# Revit family: Flooring_Entrance-Flooring_emco_MARSCHALL-Premium
name_source: partatom
category: Furniture Systems
revit_build: Autodesk Revit 2018 (Build: 20190510_1515(x64)
units: mm (PartAtom-declared; Revit-internal decimal feet)

## family parameters
Cut with Voids When Loaded = No
Host = Face
OmniClass Number = 23.15.17.11.11
OmniClass Title = Floor Toppings
Part Type = Normal
Room Calculation Point = No
Round Connector Dimension = Use Diameter
Shared = No

## types (69) — shared parameters
Assembly Code = E2010400
Date Updated = 2023/08/22
Default Elevation = 1219 mm
Description = Rollable and hard-wearing premium entrance mat with performance insert for supported installation options.
Keynote = 12480.A1
Manufacturer = Emco
Product data url = https://bimobject.com
Profile Material = Emco - Metal - Aluminium
Standard profile clearance approx. (mm) = 5 mm, rubber spacers
URL = https://www.emco-bau.com
Version = 1

## per-type parameters (varying)
| type | Brush strip | Colour fastness to artificial light ISO 105-B02 | Colour fastness to rubbing ISO 105 X12 | Colour fastness to water ISO 105 E01 | EPIMID | Flammability | Height 12 | Height 17 | Height 22 | Large | Normal | Pile material | Profile width (mm) | Scraping edge | Slip resistance | Tread surface | Weight (kg/m2) | z_Height | z_edge_height | z_insert_offset | z_insert_width | z_slot_offest | z_slot_width |
| Large With Care insert 512 PSL Care | No | good 5-6 | good 4-5 | good 4-5 | 99905 | Fire classification for the complete mat system Cfl-s1 in accordance with EN 13501 | Yes | No | No | Yes | No | 100% PA 6 (polyamide) | 46.5 mm | No | R 12 slip resistance as per DIN 51130 | The robust and exceptionally abrasion-resistant Care insert for the effective reduction of fine dirt. | 10.6 | 12 mm  [stored 0.0393701 ft] | 16 mm | 52 mm | 47 mm | 49 mm | 5 mm  [stored 0.0164042 ft] |
| Large With Care insert 517 PSL Care | No | good 5-6 | good 4-5 | good 4-5 | 99907 | Fire classification for the complete mat system Cfl-s1 in accordance with EN 13501 | No | Yes | No | Yes | No | 100% PA 6 (polyamide) | 46.5 mm | No | R 12 slip resistance as per DIN 51130 | The robust and exceptionally abrasion-resistant Care insert for the effective reduction of fine dirt. | 131 | 17 mm | 20 mm  [stored 0.0656168 ft] | 52 mm | 47 mm | 49 mm | 5 mm  [stored 0.0164042 ft] |
| Large With Conform insert 512 PSL Conform | No | - | - | - | 99911 | Fire classification for the complete mat system Cfl-s1 in accordance with EN 13501 | Yes | No | No | Yes | No | 100% PA 6 (polyamide) | 46.5 mm | No | R 12 slip resistance as per DIN 51130 | The Conform insert made of recycled materials is the perfect complement to wooden surroundings and can be used in a whole host of environments. | 10.8 | 12 mm  [stored 0.0393701 ft] | 16 mm | 52 mm | 47 mm | 49 mm | 5 mm  [stored 0.0164042 ft] |
| Large With Conform insert 517 PSL Conform | No | - | - | - | 99913 | Fire classification for the complete mat system Cfl-s1 in accordance with EN 13501 | No | Yes | No | Yes | No | 100% PA 6 (polyamide) | 46.5 mm | No | R 12 slip resistance as per DIN 51130 | The Conform insert made of recycled materials is the perfect complement to wooden surroundings and can be used in a whole host of environments. | 13.8 | 17 mm | 20 mm  [stored 0.0656168 ft] | 52 mm | 47 mm | 49 mm | 5 mm  [stored 0.0164042 ft] |
| Large With Conform insert 522 PSL Conform | No | - | - | - | 99915 | Fire classification for the complete mat system Cfl-s1 in accordance with EN 13501 | No | No | Yes | Yes | No | 100% PA 6 (polyamide) | 46.5 mm | No | R 12 slip resistance as per DIN 51130 | The Conform insert made of recycled materials is the perfect complement to wooden surroundings and can be used in a whole host of environments. | 14.5 | 22 mm  [stored 0.0721785 ft] | 25 mm  [stored 0.082021 ft] | 52 mm | 47 mm | 49 mm | 5 mm  [stored 0.0164042 ft] |
| Large With Conform insert and brush strip 517 PSL Conform B | Yes | - | - | - | 105831 | Insert with fire classification Cfl-s1 according to EN 13501. | No | Yes | No | Yes | No | 100% PA 6 (polyamide) | 46.5 mm | No | - | The Conform insert made of recycled materials is the perfect complement to wooden surroundings and can be used in a whole host of environments. The additional profile increases the cleaning power. | 131 | 17 mm | 20 mm  [stored 0.0656168 ft] | 66 mm | 47 mm | 56 mm | 20 mm  [stored 0.0656168 ft] |
| Large With Conform insert and brush strip 522 PSL Conform B | Yes | - | - | - | 105832 | Insert with fire classification Cfl-s1 according to EN 13501. | No | No | Yes | Yes | No | 100% PA 6 (polyamide) | 46.5 mm | No | - | The Conform insert made of recycled materials is the perfect complement to wooden surroundings and can be used in a whole host of environments. The additional profile increases the cleaning power. | 14.5 | 22 mm  [stored 0.0721785 ft] | 25 mm  [stored 0.082021 ft] | 66 mm | 47 mm | 56 mm | 20 mm  [stored 0.0656168 ft] |
| Large With Conform insert and scraping edge 512 PSL Conform K | No | - | - | - | 105828 | Insert with fire classification Cfl-s1 according to EN 13501. | Yes | No | No | Yes | No | 100% PA 6 (polyamide) | 46.5 mm | Yes | - | The Conform insert made of recycled materials is the perfect complement to wooden surroundings and can be used in a whole host of environments. The additional profile increases the cleaning power. | 10.5 | 12 mm  [stored 0.0393701 ft] | 16 mm | 62 mm | 47 mm | 54 mm | 15 mm  [stored 0.0492126 ft] |
| Large With Conform insert and scraping edge 517 PSL Conform K | No | - | - | - | 105829 | Insert with fire classification Cfl-s1 according to EN 13501. | No | Yes | No | Yes | No | 100% PA 6 (polyamide) | 46.5 mm | Yes | - | The Conform insert made of recycled materials is the perfect complement to wooden surroundings and can be used in a whole host of environments. The additional profile increases the cleaning power. | 13.4 | 17 mm | 20 mm  [stored 0.0656168 ft] | 62 mm | 47 mm | 54 mm | 15 mm  [stored 0.0492126 ft] |
| Large With Conform insert and scraping edge 522 PSL Conform K | No | - | - | - | 105830 | Insert with fire classification Cfl-s1 according to EN 13501. | No | No | Yes | Yes | No | 100% PA 6 (polyamide) | 46.5 mm | Yes | - | The Conform insert made of recycled materials is the perfect complement to wooden surroundings and can be used in a whole host of environments. The additional profile increases the cleaning power. | 15.2 | 22 mm  [stored 0.0721785 ft] | 25 mm  [stored 0.082021 ft] | 62 mm | 47 mm | 54 mm | 15 mm  [stored 0.0492126 ft] |
| Large With Innova insert 512 PSL Innova | No | good 5-6 | good 4-5 | good 4-5 | 99917 | Fire classification for the complete mat system Cfl-s1 in accordance with EN 13501 | Yes | No | No | Yes | No | 100% PA 6 (polyamide) | 46.5 mm | No | R 12 slip resistance as per DIN 51130 | The exceptionally flexible Innova insert not only creates a sophisticated impression but also improves room acoustics. | 10.9 | 12 mm  [stored 0.0393701 ft] | 16 mm | 52 mm | 47 mm | 49 mm | 5 mm  [stored 0.0164042 ft] |
| Large With Innova insert 517 PSL Innova | No | good 5-6 | good 4-5 | good 4-5 | 99919 | Fire classification for the complete mat system Cfl-s1 in accordance with EN 13501 | No | Yes | No | Yes | No | 100% PA 6 (polyamide) | 46.5 mm | No | R 12 slip resistance as per DIN 51130 | The exceptionally flexible Innova insert not only creates a sophisticated impression but also improves room acoustics. | 12.9 | 17 mm | 20 mm  [stored 0.0656168 ft] | 52 mm | 47 mm | 49 mm | 5 mm  [stored 0.0164042 ft] |
| Large With Innova insert 522 PSL Innova | No | good 5-6 | good 4-5 | good 4-5 | 99921 | Fire classification for the complete mat system Cfl-s1 in accordance with EN 13501 | No | No | Yes | Yes | No | 100% PA 6 (polyamide) | 46.5 mm | No | R 12 slip resistance as per DIN 51130 | The exceptionally flexible Innova insert not only creates a sophisticated impression but also improves room acoustics. | 141 | 22 mm  [stored 0.0721785 ft] | 25 mm  [stored 0.082021 ft] | 52 mm | 47 mm | 49 mm | 5 mm  [stored 0.0164042 ft] |
| Large With Innova insert and brush strip 517 PSL Innova B | Yes | - | - | - | 105841 | Insert with fire classification Cfl-s1 according to EN 13501. | No | Yes | No | Yes | No | 100% PA 6 (polyamide) | 46.5 mm | No | - | The exceptionally flexible Innova insert not only creates a sophisticated impression but also improves room acoustics. The additional profile increases the cleaning power. | 12.8 | 17 mm | 20 mm  [stored 0.0656168 ft] | 66 mm | 47 mm | 56 mm | 20 mm  [stored 0.0656168 ft] |
| Large With Innova insert and brush strip 522 PSL Innova B | Yes | - | - | - | 105842 | Insert with fire classification Cfl-s1 according to EN 13501. | No | No | Yes | Yes | No | 100% PA 6 (polyamide) | 46.5 mm | No | - | The exceptionally flexible Innova insert not only creates a sophisticated impression but also improves room acoustics. The additional profile increases the cleaning power. | 142 | 22 mm  [stored 0.0721785 ft] | 25 mm  [stored 0.082021 ft] | 66 mm | 47 mm | 56 mm | 20 mm  [stored 0.0656168 ft] |
| Large With Innova insert and scraping edge 512 PSL Innova K | No | - | - | - | 105838 | Insert with fire classification Cfl-s1 according to EN 13501. | Yes | No | No | Yes | No | 100% PA 6 (polyamide) | 46.5 mm | Yes | - | The exceptionally flexible Innova insert not only creates a sophisticated impression but also improves room acoustics. The additional profile increases the cleaning power. | 10.3 | 12 mm  [stored 0.0393701 ft] | 16 mm | 62 mm | 47 mm | 54 mm | 15 mm  [stored 0.0492126 ft] |
| Large With Innova insert and scraping edge 517 PSL Innova K | No | - | - | - | 105839 | Insert with fire classification Cfl-s1 according to EN 13501. | No | Yes | No | Yes | No | 100% PA 6 (polyamide) | 46.5 mm | Yes | - | The exceptionally flexible Innova insert not only creates a sophisticated impression but also improves room acoustics. The additional profile increases the cleaning power. | 131 | 17 mm | 20 mm  [stored 0.0656168 ft] | 62 mm | 47 mm | 54 mm | 15 mm  [stored 0.0492126 ft] |
| Large With Innova insert and scraping edge 522 PSL Innova K | No | - | - | - | 105840 | Insert with fire classification Cfl-s1 according to EN 13501. | No | No | Yes | Yes | No | 100% PA 6 (polyamide) | 46.5 mm | Yes | - | The exceptionally flexible Innova insert not only creates a sophisticated impression but also improves room acoustics. The additional profile increases the cleaning power. | 14.9 | 22 mm  [stored 0.0721785 ft] | 25 mm  [stored 0.082021 ft] | 62 mm | 47 mm | 54 mm | 15 mm  [stored 0.0492126 ft] |
| Large With Maximus insert and brush strip 517 PSL Maximus B | Yes | - | - | - | 105819 | Insert with fire classification Bfl-s1 according to EN 13501. | No | Yes | No | Yes | No | 100% PA 6.6 (polyamide) | 46.5 mm | No | - | Embedded, robust MAXIMUS inserts in Bfl-S1 quality (clean-off floor covering made from special polyamide yarn, 100%) | 13 | 17 mm | 20 mm  [stored 0.0656168 ft] | 66 mm | 47 mm | 56 mm | 20 mm  [stored 0.0656168 ft] |
| Large With Maximus insert and brush strip 517 PSL Maximus Image B | Yes | - | - | - | 105820 | Insert with fire classification Bfl-s1 according to EN 13501. | No | Yes | No | Yes | No | 100% PA 6.6 (polyamide) | 46.5 mm | No | - | Embedded, robust MAXIMUS inserts in Bfl-S1 quality (clean-off floor covering made from special polyamide yarn, 100%) | 13 | 17 mm | 20 mm  [stored 0.0656168 ft] | 66 mm | 47 mm | 56 mm | 20 mm  [stored 0.0656168 ft] |
| Large With Maximus insert and brush strip 522 PSL Maximus B | Yes | - | - | - | 105821 | Insert with fire classification Bfl-s1 according to EN 13501. | No | No | Yes | Yes | No | 100% PA 6.6 (polyamide) | 46.5 mm | No | - | Embedded, robust MAXIMUS inserts in Bfl-S1 quality (clean-off floor covering made from special polyamide yarn, 100%) | 14.4 | 22 mm  [stored 0.0721785 ft] | 25 mm  [stored 0.082021 ft] | 66 mm | 47 mm | 56 mm | 20 mm  [stored 0.0656168 ft] |
| Large With Maximus insert and brush strip 522 PSL Maximus Image B | Yes | - | - | - | 105822 | Insert with fire classification Bfl-s1 according to EN 13501. | No | No | Yes | Yes | No | 100% PA 6.6 (polyamide) | 46.5 mm | No | - | Embedded, robust MAXIMUS inserts in Bfl-S1 quality (clean-off floor covering made from special polyamide yarn, 100%) | 14.4 | 22 mm  [stored 0.0721785 ft] | 25 mm  [stored 0.082021 ft] | 66 mm | 47 mm | 56 mm | 20 mm  [stored 0.0656168 ft] |
| Large With Maximus insert and scraping edge 512 PSL Maximus Image K | No | - | - | - | 105814 | Insert with fire classification Bfl-s1 according to EN 13501. | Yes | No | No | Yes | No | 100% PA 6.6 (polyamide) | 46.5 mm | Yes | - | Embedded, robust MAXIMUS inserts in Bfl-S1 quality (clean-off floor covering made from special polyamide yarn, 100%) | 10.9 | 12 mm  [stored 0.0393701 ft] | 16 mm | 62 mm | 47 mm | 54 mm | 15 mm  [stored 0.0492126 ft] |
| Large With Maximus insert and scraping edge 512 PSL Maximus K | No | - | - | - | 105813 | Insert with fire classification Bfl-s1 according to EN 13501. | Yes | No | No | Yes | No | 100% PA 6.6 (polyamide) | 46.5 mm | Yes | - | Embedded, robust MAXIMUS inserts in Bfl-S1 quality (clean-off floor covering made from special polyamide yarn, 100%) | 10.9 | 12 mm  [stored 0.0393701 ft] | 16 mm | 62 mm | 47 mm | 54 mm | 15 mm  [stored 0.0492126 ft] |
| Large With Maximus insert and scraping edge 517 PSL Maximus Image K | No | - | - | - | 105816 | Insert with fire classification Bfl-s1 according to EN 13501. | No | Yes | No | Yes | No | 100% PA 6.6 (polyamide) | 46.5 mm | Yes | - | Embedded, robust MAXIMUS inserts in Bfl-S1 quality (clean-off floor covering made from special polyamide yarn, 100%) | 13.9 | 17 mm | 20 mm  [stored 0.0656168 ft] | 62 mm | 47 mm | 54 mm | 15 mm  [stored 0.0492126 ft] |
| Large With Maximus insert and scraping edge 517 PSL Maximus K | No | - | - | - | 105815 | Insert with fire classification Bfl-s1 according to EN 13501. | No | Yes | No | Yes | No | 100% PA 6.6 (polyamide) | 46.5 mm | Yes | - | Embedded, robust MAXIMUS inserts in Bfl-S1 quality (clean-off floor covering made from special polyamide yarn, 100%) | 13.9 | 17 mm | 20 mm  [stored 0.0656168 ft] | 62 mm | 47 mm | 54 mm | 15 mm  [stored 0.0492126 ft] |
| Large With Maximus insert and scraping edge 522 PSL Maximus Image K | No | - | - | - | 105818 | Insert with fire classification Bfl-s1 according to EN 13501. | No | No | Yes | Yes | No | 100% PA 6.6 (polyamide) | 46.5 mm | Yes | - | Embedded, robust MAXIMUS inserts in Bfl-S1 quality (clean-off floor covering made from special polyamide yarn, 100%) | 15.8 | 22 mm  [stored 0.0721785 ft] | 25 mm  [stored 0.082021 ft] | 62 mm | 47 mm | 54 mm | 15 mm  [stored 0.0492126 ft] |
| Large With Maximus insert and scraping edge 522 PSL Maximus K | No | - | - | - | 105817 | Insert with fire classification Bfl-s1 according to EN 13501. | No | No | Yes | Yes | No | 100% PA 6.6 (polyamide) | 46.5 mm | Yes | - | Embedded, robust MAXIMUS inserts in Bfl-S1 quality (clean-off floor covering made from special polyamide yarn, 100%) | 15.8 | 22 mm  [stored 0.0721785 ft] | 25 mm  [stored 0.082021 ft] | 62 mm | 47 mm | 54 mm | 15 mm  [stored 0.0492126 ft] |
| Large With Outdoor insert 512 PSL Outdoor | No | excellent 7 | good 4-5 | good 4-5 | 99931 | Fire classification for the complete mat system Cfl-s1 in accordance with EN 13501 | Yes | No | No | Yes | No | 100% PA 6 (polyamide) | 46.5 mm | No | R 11 slip resistance as per DIN 51130 | The weather-resistant Outdoor insert for noticeably thorough removal of coarse dirt. | 10.1 | 12 mm  [stored 0.0393701 ft] | 16 mm | 52 mm | 47 mm | 49 mm | 5 mm  [stored 0.0164042 ft] |
| Large With Outdoor insert 517 PSL Outdoor | No | excellent 7 | good 4-5 | good 4-5 | 99933 | Fire classification for the complete mat system Cfl-s1 in accordance with EN 13501 | No | Yes | No | Yes | No | 100% PA 6 (polyamide) | 46.5 mm | No | R 11 slip resistance as per DIN 51130 | The weather-resistant Outdoor insert for noticeably thorough removal of coarse dirt. | 12.6 | 17 mm | 20 mm  [stored 0.0656168 ft] | 52 mm | 47 mm | 49 mm | 5 mm  [stored 0.0164042 ft] |
| Large With Outdoor insert 522 PSL Outdoor | No | excellent 7 | good 4-5 | good 4-5 | 99935 | Fire classification for the complete mat system Cfl-s1 in accordance with EN 13501 | No | No | Yes | Yes | No | 100% PA 6 (polyamide) | 46.5 mm | No | R 11 slip resistance as per DIN 51130 | The weather-resistant Outdoor insert for noticeably thorough removal of coarse dirt. | 13.8 | 22 mm  [stored 0.0721785 ft] | 25 mm  [stored 0.082021 ft] | 52 mm | 47 mm | 49 mm | 5 mm  [stored 0.0164042 ft] |
| Large With Outdoor insert and brush strip 517 PSL Outdoor B | Yes | - | - | - | 105861 | Insert with fire classification Cfl-s1 according to EN 13501. | No | Yes | No | Yes | No | 100% PA 6 (polyamide) | 46.5 mm | No | - | The weather-resistant Outdoor insert for noticeably thorough removal of coarse dirt. The additional profile increases the cleaning power. | 13.3 | 17 mm | 20 mm  [stored 0.0656168 ft] | 66 mm | 47 mm | 56 mm | 20 mm  [stored 0.0656168 ft] |
| Large With Outdoor insert and brush strip 522 PSL Outdoor B | Yes | - | - | - | 105862 | Insert with fire classification Cfl-s1 according to EN 13501. | No | No | Yes | Yes | No | 100% PA 6 (polyamide) | 46.5 mm | No | - | The weather-resistant Outdoor insert for noticeably thorough removal of coarse dirt. The additional profile increases the cleaning power. | 14 | 22 mm  [stored 0.0721785 ft] | 25 mm  [stored 0.082021 ft] | 66 mm | 47 mm | 56 mm | 20 mm  [stored 0.0656168 ft] |
| Large With Outdoor insert and scraping edge 512 PSL Outdoor K | No | - | - | - | 105858 | Insert with fire classification Cfl-s1 according to EN 13501. | Yes | No | No | Yes | No | 100% PA 6 (polyamide) | 46.5 mm | Yes | - | The weather-resistant Outdoor insert for noticeably thorough removal of coarse dirt. The additional profile increases the cleaning power. | 10 | 12 mm  [stored 0.0393701 ft] | 16 mm | 62 mm | 47 mm | 54 mm | 15 mm  [stored 0.0492126 ft] |
| Large With Outdoor insert and scraping edge 517 PSL Outdoor K | No | - | - | - | 105859 | Insert with fire classification Cfl-s1 according to EN 13501. | No | Yes | No | Yes | No | 100% PA 6 (polyamide) | 46.5 mm | Yes | - | The weather-resistant Outdoor insert for noticeably thorough removal of coarse dirt. The additional profile increases the cleaning power. | 12.9 | 17 mm | 20 mm  [stored 0.0656168 ft] | 62 mm | 47 mm | 54 mm | 15 mm  [stored 0.0492126 ft] |
| Large With Outdoor insert and scraping edge 522 PSL Outdoor K | No | - | - | - | 105860 | Insert with fire classification Cfl-s1 according to EN 13501. | No | No | Yes | Yes | No | 100% PA 6 (polyamide) | 46.5 mm | Yes | - | The weather-resistant Outdoor insert for noticeably thorough removal of coarse dirt. The additional profile increases the cleaning power. | 14.7 | 22 mm  [stored 0.0721785 ft] | 25 mm  [stored 0.082021 ft] | 62 mm | 47 mm | 54 mm | 15 mm  [stored 0.0492126 ft] |
| With Care insert 512 PS Care | No | good 5-6 | good 4-5 | good 4-5 | 99904 | Fire classification for the complete mat system Cfl-s1 in accordance with EN 13501 | Yes | No | No | No | Yes | 100% PA 6 (polyamide) | 30 mm | No | R 12 slip resistance as per DIN 51130 | The robust and exceptionally abrasion-resistant Care insert for the effective reduction of fine dirt. | 12 | 12 mm  [stored 0.0393701 ft] | 16 mm | 35 mm  [stored 0.114829 ft] | 30 mm  [stored 0.0984252 ft] | 33 mm | 5 mm  [stored 0.0164042 ft] |
| With Care insert 517 PS Care | No | good 5-6 | good 4-5 | good 4-5 | 99906 | Fire classification for the complete mat system Cfl-s1 in accordance with EN 13501 | No | Yes | No | No | Yes | 100% PA 6 (polyamide) | 30 mm | No | R 12 slip resistance as per DIN 51130 | The robust and exceptionally abrasion-resistant Care insert for the effective reduction of fine dirt. | 14.7 | 17 mm | 20 mm  [stored 0.0656168 ft] | 35 mm  [stored 0.114829 ft] | 30 mm  [stored 0.0984252 ft] | 33 mm | 5 mm  [stored 0.0164042 ft] |
| With Care insert 522 PS Care | No | good 5-6 | good 4-5 | good 4-5 | 99908 | Fire classification for the complete mat system Cfl-s1 in accordance with EN 13501 | No | No | Yes | No | Yes | 100% PA 6 (polyamide) | 30 mm | No | R 12 slip resistance as per DIN 51130 | The robust and exceptionally abrasion-resistant Care insert for the effective reduction of fine dirt. | 16.8 | 22 mm  [stored 0.0721785 ft] | 25 mm  [stored 0.082021 ft] | 35 mm  [stored 0.114829 ft] | 30 mm  [stored 0.0984252 ft] | 33 mm | 5 mm  [stored 0.0164042 ft] |
| With Conform insert 512 PS Conform | No | - | - | - | 99910 | Fire classification for the complete mat system Cfl-s1 in accordance with EN 13501 | Yes | No | No | No | Yes | 100% PA 6 (polyamide) | 30 mm | No | R 12 slip resistance as per DIN 51130 | The Conform insert made of recycled materials is the perfect complement to wooden surroundings and can be used in a whole host of environments. | 121 | 12 mm  [stored 0.0393701 ft] | 16 mm | 35 mm  [stored 0.114829 ft] | 30 mm  [stored 0.0984252 ft] | 33 mm | 5 mm  [stored 0.0164042 ft] |
| With Conform insert 517 PS Conform | No | - | - | - | 99912 | Fire classification for the complete mat system Cfl-s1 in accordance with EN 13501 | No | Yes | No | No | Yes | 100% PA 6 (polyamide) | 30 mm | No | R 12 slip resistance as per DIN 51130 | The Conform insert made of recycled materials is the perfect complement to wooden surroundings and can be used in a whole host of environments. | 14.8 | 17 mm | 20 mm  [stored 0.0656168 ft] | 35 mm  [stored 0.114829 ft] | 30 mm  [stored 0.0984252 ft] | 33 mm | 5 mm  [stored 0.0164042 ft] |
| With Conform insert 522 PS Conform | No | - | - | - | 99914 | Fire classification for the complete mat system Cfl-s1 in accordance with EN 13501 | No | No | Yes | No | Yes | 100% PA 6 (polyamide) | 30 mm | No | R 12 slip resistance as per DIN 51130 | The Conform insert made of recycled materials is the perfect complement to wooden surroundings and can be used in a whole host of environments. | 17 | 22 mm  [stored 0.0721785 ft] | 25 mm  [stored 0.082021 ft] | 35 mm  [stored 0.114829 ft] | 30 mm  [stored 0.0984252 ft] | 33 mm | 5 mm  [stored 0.0164042 ft] |
| With Conform insert and brush strip 517 PS Conform B | Yes | - | - | - | 105826 | Insert with fire classification Cfl-s1 according to EN 13501. | No | Yes | No | No | Yes | 100% PA 6 (polyamide) | 30 mm | No | - | The Conform insert made of recycled materials is the perfect complement to wooden surroundings and can be used in a whole host of environments. The additional profile increases the cleaning power. | 13.9 | 17 mm | 20 mm  [stored 0.0656168 ft] | 50 mm | 30 mm  [stored 0.0984252 ft] | 40 mm  [stored 0.131234 ft] | 20 mm  [stored 0.0656168 ft] |
| With Conform insert and brush strip 522 PS Conform B | Yes | - | - | - | 105827 | Insert with fire classification Cfl-s1 according to EN 13501. | No | No | Yes | No | Yes | 100% PA 6 (polyamide) | 30 mm | No | - | The Conform insert made of recycled materials is the perfect complement to wooden surroundings and can be used in a whole host of environments. The additional profile increases the cleaning power. | 15.2 | 22 mm  [stored 0.0721785 ft] | 25 mm  [stored 0.082021 ft] | 50 mm | 30 mm  [stored 0.0984252 ft] | 40 mm  [stored 0.131234 ft] | 20 mm  [stored 0.0656168 ft] |
| With Conform insert and scraping edge 512 PS Conform K | No | - | - | - | 105823 | Insert with fire classification Cfl-s1 according to EN 13501. | Yes | No | No | No | Yes | 100% PA 6 (polyamide) | 30 mm | Yes | - | The Conform insert made of recycled materials is the perfect complement to wooden surroundings and can be used in a whole host of environments. The additional profile increases the cleaning power. | 11.7 | 12 mm  [stored 0.0393701 ft] | 16 mm | 45 mm | 30 mm  [stored 0.0984252 ft] | 38 mm | 15 mm  [stored 0.0492126 ft] |
| With Conform insert and scraping edge 517 PS Conform K | No | - | - | - | 105824 | Insert with fire classification Cfl-s1 according to EN 13501. | No | Yes | No | No | Yes | 100% PA 6 (polyamide) | 30 mm | Yes | - | The Conform insert made of recycled materials is the perfect complement to wooden surroundings and can be used in a whole host of environments. The additional profile increases the cleaning power. | 14.3 | 17 mm | 20 mm  [stored 0.0656168 ft] | 45 mm | 30 mm  [stored 0.0984252 ft] | 38 mm | 15 mm  [stored 0.0492126 ft] |
| With Conform insert and scraping edge 522 PS Conform K | No | - | - | - | 105825 | Insert with fire classification Cfl-s1 according to EN 13501. | No | No | Yes | No | Yes | 100% PA 6 (polyamide) | 30 mm | Yes | - | The Conform insert made of recycled materials is the perfect complement to wooden surroundings and can be used in a whole host of environments. The additional profile increases the cleaning power. | 16.8 | 22 mm  [stored 0.0721785 ft] | 25 mm  [stored 0.082021 ft] | 45 mm | 30 mm  [stored 0.0984252 ft] | 38 mm | 15 mm  [stored 0.0492126 ft] |
| With Innova insert 512 PS Innova | No | good 5-6 | good 4-5 | good 4-5 | 99916 | Fire classification for the complete mat system Cfl-s1 in accordance with EN 13501 | Yes | No | No | No | Yes | 100% PA 6 (polyamide) | 30 mm | No | R 12 slip resistance as per DIN 51130 | The exceptionally flexible Innova insert not only creates a sophisticated impression but also improves room acoustics. | 12 | 12 mm  [stored 0.0393701 ft] | 16 mm | 35 mm  [stored 0.114829 ft] | 30 mm  [stored 0.0984252 ft] | 33 mm | 5 mm  [stored 0.0164042 ft] |
| With Innova insert 517 PS Innova | No | good 5-6 | good 4-5 | good 4-5 | 99918 | Fire classification for the complete mat system Cfl-s1 in accordance with EN 13501 | No | Yes | No | No | Yes | 100% PA 6 (polyamide) | 30 mm | No | R 12 slip resistance as per DIN 51130 | The exceptionally flexible Innova insert not only creates a sophisticated impression but also improves room acoustics. | 14.7 | 17 mm | 20 mm  [stored 0.0656168 ft] | 35 mm  [stored 0.114829 ft] | 30 mm  [stored 0.0984252 ft] | 33 mm | 5 mm  [stored 0.0164042 ft] |
| With Innova insert 522 PS Innova | No | good 5-6 | good 4-5 | good 4-5 | 99920 | Fire classification for the complete mat system Cfl-s1 in accordance with EN 13501 | No | No | Yes | No | Yes | 100% PA 6 (polyamide) | 30 mm | No | R 12 slip resistance as per DIN 51130 | The exceptionally flexible Innova insert not only creates a sophisticated impression but also improves room acoustics. | 16.8 | 22 mm  [stored 0.0721785 ft] | 25 mm  [stored 0.082021 ft] | 35 mm  [stored 0.114829 ft] | 30 mm  [stored 0.0984252 ft] | 33 mm | 5 mm  [stored 0.0164042 ft] |
| With Innova insert and brush strip 517 PS Innova B | Yes | - | - | - | 105836 | Insert with fire classification Cfl-s1 according to EN 13501. | No | Yes | No | No | Yes | 100% PA 6 (polyamide) | 30 mm | No | - | The exceptionally flexible Innova insert not only creates a sophisticated impression but also improves room acoustics. The additional profile increases the cleaning power. | 13.2 | 17 mm | 20 mm  [stored 0.0656168 ft] | 50 mm | 30 mm  [stored 0.0984252 ft] | 40 mm  [stored 0.131234 ft] | 20 mm  [stored 0.0656168 ft] |
| With Innova insert and brush strip 522 PS Innova B | Yes | - | - | - | 105837 | Insert with fire classification Cfl-s1 according to EN 13501. | No | No | Yes | No | Yes | 100% PA 6 (polyamide) | 30 mm | No | - | The exceptionally flexible Innova insert not only creates a sophisticated impression but also improves room acoustics. The additional profile increases the cleaning power. | 15.1 | 22 mm  [stored 0.0721785 ft] | 25 mm  [stored 0.082021 ft] | 50 mm | 30 mm  [stored 0.0984252 ft] | 40 mm  [stored 0.131234 ft] | 20 mm  [stored 0.0656168 ft] |
| With Innova insert and scraping edge 512 PS Innova K | No | - | - | - | 105833 | Insert with fire classification Cfl-s1 according to EN 13501. | Yes | No | No | No | Yes | 100% PA 6 (polyamide) | 30 mm | Yes | - | The exceptionally flexible Innova insert not only creates a sophisticated impression but also improves room acoustics. The additional profile increases the cleaning power. | 11.5 | 12 mm  [stored 0.0393701 ft] | 16 mm | 45 mm | 30 mm  [stored 0.0984252 ft] | 38 mm | 15 mm  [stored 0.0492126 ft] |
| With Innova insert and scraping edge 517 PS Innova K | No | - | - | - | 105834 | Insert with fire classification Cfl-s1 according to EN 13501. | No | Yes | No | No | Yes | 100% PA 6 (polyamide) | 30 mm | Yes | - | The exceptionally flexible Innova insert not only creates a sophisticated impression but also improves room acoustics. The additional profile increases the cleaning power. | 141 | 17 mm | 20 mm  [stored 0.0656168 ft] | 45 mm | 30 mm  [stored 0.0984252 ft] | 38 mm | 15 mm  [stored 0.0492126 ft] |
| With Innova insert and scraping edge 522 PS Innova K | No | - | - | - | 105835 | Insert with fire classification Cfl-s1 according to EN 13501. | No | No | Yes | No | Yes | 100% PA 6 (polyamide) | 30 mm | Yes | - | The exceptionally flexible Innova insert not only creates a sophisticated impression but also improves room acoustics. The additional profile increases the cleaning power. | 16.8 | 22 mm  [stored 0.0721785 ft] | 25 mm  [stored 0.082021 ft] | 45 mm | 30 mm  [stored 0.0984252 ft] | 38 mm | 15 mm  [stored 0.0492126 ft] |
| With Maximus Image insert and scraping edge 512 PS Maximus Image K | No | - | - | - | 105804 | Insert with fire classification Bfl-s1 according to EN 13501. | Yes | No | No | No | Yes | 100% PA 6.6 (polyamide) | 30 mm | Yes | - | Embedded, robust MAXIMUS inserts in Bfl-S1 quality (clean-off floor covering made from special polyamide yarn, 100%) | 11.6 | 12 mm  [stored 0.0393701 ft] | 16 mm | 45 mm | 30 mm  [stored 0.0984252 ft] | 38 mm | 15 mm  [stored 0.0492126 ft] |
| With Maximus Image insert and scraping edge 517 PS Maximus Image K | No | - | - | - | 105806 | Insert with fire classification Bfl-s1 according to EN 13501. | No | Yes | No | No | Yes | 100% PA 6.6 (polyamide) | 30 mm | Yes | - | Embedded, robust MAXIMUS inserts in Bfl-S1 quality (clean-off floor covering made from special polyamide yarn, 100%) | 142 | 17 mm | 20 mm  [stored 0.0656168 ft] | 45 mm | 30 mm  [stored 0.0984252 ft] | 38 mm | 15 mm  [stored 0.0492126 ft] |
| With Maximus Image insert and scraping edge 522 PS Maximus Image K | No | - | - | - | 105807 | Insert with fire classification Bfl-s1 according to EN 13501. | No | No | Yes | No | Yes | 100% PA 6.6 (polyamide) | 30 mm | Yes | - | Embedded, robust MAXIMUS inserts in Bfl-S1 quality (clean-off floor covering made from special polyamide yarn, 100%) | 16.8 | 22 mm  [stored 0.0721785 ft] | 25 mm  [stored 0.082021 ft] | 45 mm | 30 mm  [stored 0.0984252 ft] | 38 mm | 15 mm  [stored 0.0492126 ft] |
| With Maximus insert and scraping edge 512 PS Maximus K | No | - | - | - | 105803 | Insert with fire classification Bfl-s1 according to EN 13501. | Yes | No | No | No | Yes | 100% PA 6.6 (polyamide) | 30 mm | Yes | - | Embedded, robust MAXIMUS inserts in Bfl-S1 quality (clean-off floor covering made from special polyamide yarn, 100%) | 11.6 | 12 mm  [stored 0.0393701 ft] | 16 mm | 45 mm | 30 mm  [stored 0.0984252 ft] | 38 mm | 15 mm  [stored 0.0492126 ft] |
| With Maximus insert and scraping edge 517 PS Maximus K | No | - | - | - | 105805 | Insert with fire classification Bfl-s1 according to EN 13501. | No | Yes | No | No | Yes | 100% PA 6.6 (polyamide) | 30 mm | Yes | - | Embedded, robust MAXIMUS inserts in Bfl-S1 quality (clean-off floor covering made from special polyamide yarn, 100%) | 142 | 17 mm | 20 mm  [stored 0.0656168 ft] | 45 mm | 30 mm  [stored 0.0984252 ft] | 38 mm | 15 mm  [stored 0.0492126 ft] |
| With Maximus insert and scraping edge 522 PS Maximus K | No | - | - | - | 105812 | Insert with fire classification Bfl-s1 according to EN 13501. | No | No | Yes | No | Yes | 100% PA 6.6 (polyamide) | 30 mm | Yes | - | Embedded, robust MAXIMUS inserts in Bfl-S1 quality (clean-off floor covering made from special polyamide yarn, 100%) | 16.8 | 22 mm  [stored 0.0721785 ft] | 25 mm  [stored 0.082021 ft] | 45 mm | 30 mm  [stored 0.0984252 ft] | 38 mm | 15 mm  [stored 0.0492126 ft] |
| With Outdoor insert 512 PS Outdoor | No | excellent 7 | good 4-5 | good 4-5 | 99930 | Fire classification for the complete mat system Cfl-s1 in accordance with EN 13501 | Yes | No | No | No | Yes | 100% PA 6 (polyamide) | 30 mm | No | R 11 slip resistance as per DIN 51130 | The weather-resistant Outdoor insert for noticeably thorough removal of coarse dirt. | 11.6 | 12 mm  [stored 0.0393701 ft] | 16 mm | 35 mm  [stored 0.114829 ft] | 30 mm  [stored 0.0984252 ft] | 33 mm | 5 mm  [stored 0.0164042 ft] |
| With Outdoor insert 517 PS Outdoor | No | excellent 7 | good 4-5 | good 4-5 | 99932 | Fire classification for the complete mat system Cfl-s1 in accordance with EN 13501 | No | Yes | No | No | Yes | 100% PA 6 (polyamide) | 30 mm | No | R 11 slip resistance as per DIN 51130 | The weather-resistant Outdoor insert for noticeably thorough removal of coarse dirt. | 14.3 | 17 mm | 20 mm  [stored 0.0656168 ft] | 35 mm  [stored 0.114829 ft] | 30 mm  [stored 0.0984252 ft] | 33 mm | 5 mm  [stored 0.0164042 ft] |
| With Outdoor insert 522 PS Outdoor | No | excellent 7 | good 4-5 | good 4-5 | 99934 | Fire classification for the complete mat system Cfl-s1 in accordance with EN 13501 | No | No | Yes | No | Yes | 100% PA 6 (polyamide) | 30 mm | No | R 11 slip resistance as per DIN 51130 | The weather-resistant Outdoor insert for noticeably thorough removal of coarse dirt. | 16.5 | 22 mm  [stored 0.0721785 ft] | 25 mm  [stored 0.082021 ft] | 35 mm  [stored 0.114829 ft] | 30 mm  [stored 0.0984252 ft] | 33 mm | 5 mm  [stored 0.0164042 ft] |
| With Outdoor insert and brush strip 517 PS Outdoor B | Yes | - | - | - | 105856 | Insert with fire classification Cfl-s1 according to EN 13501. | No | Yes | No | No | Yes | 100% PA 6 (polyamide) | 30 mm | No | - | The weather-resistant Outdoor insert for noticeably thorough removal of coarse dirt. The additional profile increases the cleaning power. | 12.9 | 17 mm | 20 mm  [stored 0.0656168 ft] | 50 mm | 30 mm  [stored 0.0984252 ft] | 40 mm  [stored 0.131234 ft] | 20 mm  [stored 0.0656168 ft] |
| With Outdoor insert and brush strip 522 PS Outdoor B | Yes | - | - | - | 105857 | Insert with fire classification Cfl-s1 according to EN 13501. | No | No | Yes | No | Yes | 100% PA 6 (polyamide) | 30 mm | No | - | The weather-resistant Outdoor insert for noticeably thorough removal of coarse dirt. The additional profile increases the cleaning power. | 14.9 | 22 mm  [stored 0.0721785 ft] | 25 mm  [stored 0.082021 ft] | 50 mm | 30 mm  [stored 0.0984252 ft] | 40 mm  [stored 0.131234 ft] | 20 mm  [stored 0.0656168 ft] |
| With Outdoor insert and scraping edge 512 PS Outdoor K | No | - | - | - | 105853 | Insert with fire classification Cfl-s1 according to EN 13501. | Yes | No | No | No | Yes | 100% PA 6 (polyamide) | 30 mm | Yes | - | The weather-resistant Outdoor insert for noticeably thorough removal of coarse dirt. The additional profile increases the cleaning power. | 11.3 | 12 mm  [stored 0.0393701 ft] | 16 mm | 45 mm | 30 mm  [stored 0.0984252 ft] | 38 mm | 15 mm  [stored 0.0492126 ft] |
| With Outdoor insert and scraping edge 517 PS Outdoor K | No | - | - | - | 105854 | Insert with fire classification Cfl-s1 according to EN 13501. | No | Yes | No | No | Yes | 100% PA 6 (polyamide) | 30 mm | Yes | - | The weather-resistant Outdoor insert for noticeably thorough removal of coarse dirt. The additional profile increases the cleaning power. | 13.9 | 17 mm | 20 mm  [stored 0.0656168 ft] | 45 mm | 30 mm  [stored 0.0984252 ft] | 38 mm | 15 mm  [stored 0.0492126 ft] |
| With Outdoor insert and scraping edge 522 PS Outdoor K | No | - | - | - | 105855 | Insert with fire classification Cfl-s1 according to EN 13501. | No | No | Yes | No | Yes | 100% PA 6 (polyamide) | 30 mm | Yes | - | The weather-resistant Outdoor insert for noticeably thorough removal of coarse dirt. The additional profile increases the cleaning power. | 16.5 | 22 mm  [stored 0.0721785 ft] | 25 mm  [stored 0.082021 ft] | 45 mm | 30 mm  [stored 0.0984252 ft] | 38 mm | 15 mm  [stored 0.0492126 ft] |

note: column(s) folded — value = type name in every type: Model

note: [stored X ft] marks values corroborated as IEEE doubles in the binary element streams (Revit-internal decimal feet)

## geometry (parser evidence)
native form markers: Sweep x6
no freeform markers — native parametric forms only
